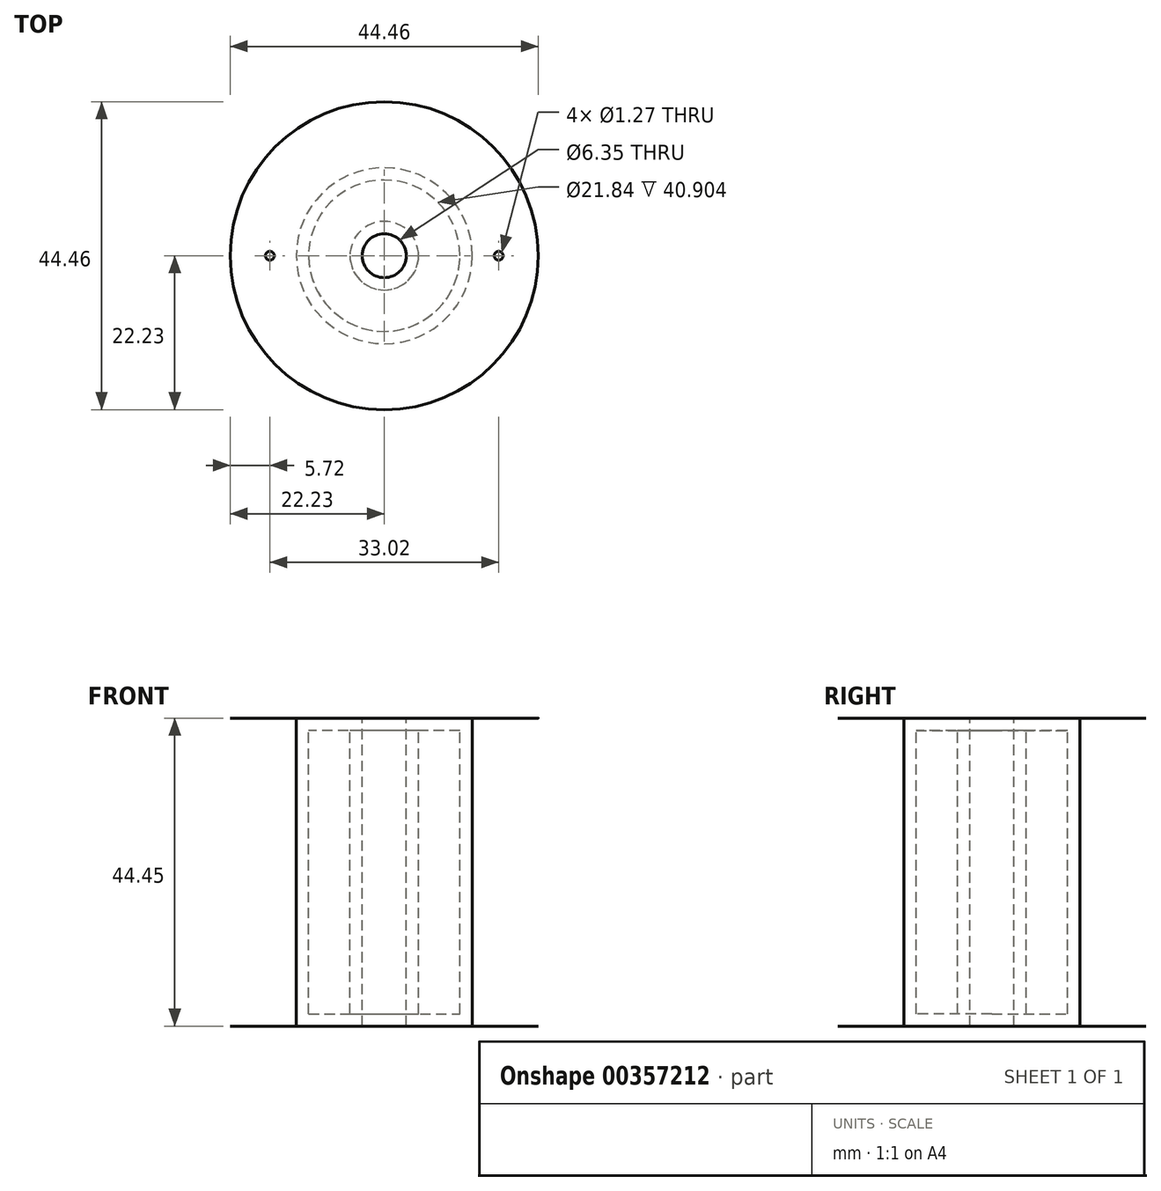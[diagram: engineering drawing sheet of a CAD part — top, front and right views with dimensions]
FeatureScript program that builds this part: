
annotation { "Feature Type Name" : "Feature", "Feature Type Description" : "" }
export const myFeature = defineFeature(function(context is Context, id is Id, definition is map)
    precondition{}
    {
        {
            var Q0;
            Q0=qCreatedBy(makeId("Top.planeOp"),FACE);
            var sketch = newSketch(context, id + "F0", { "sketchPlane" : qUnion([Q0])});
            skCircle(sketch, "E0", {"center": v(0, 0) * mm, "radius": 22.23 * mm});
            skSolve(sketch);
        }
        {
            var Q0;
            Q0=makeQuery(id+"F0.imprint","IMPRINT",FACE,{"disambiguationData":[TD([[makeQuery(id+"F0.imprint","IMPRINT",EDGE,{"derivedFrom":sQuery(id+"F0.wireOp",EDGE,"E0")}),1.0]])]});
            extrude(context, id + "F1", {"entities" : qUnion([Q0]), "depth" : 1 / 203.2 * mm});
        }
        {
            var Q0;
            Q0=makeQuery(id+"F1.opExtrude","CAP_FACE",FACE,{"disambiguationData":[OSD([sQuery(id+"F0.wireOp",EDGE,"E0")])],"isStart":true});
            var sketch = newSketch(context, id + "F2", { "sketchPlane" : qUnion([Q0])});
            skCircle(sketch, "E1", {"center": v(0, 0) * mm, "radius": 12.7 * mm});
            skSolve(sketch);
        }
        {
            var Q0;
            Q0 = qSketchRegion(id + "F2", true);
            extrude(context, id + "F3", {"entities" : qUnion([Q0]), "operationType" : NewBodyOperationType.ADD, "depth" : 44.45 * mm});
        }
        {
            var Q0;
            Q0=makeQuery(id+"F3.opExtrude","CAP_FACE",FACE,{"disambiguationData":[OSD([sQuery(id+"F2.wireOp",EDGE,"E1")])],"isStart":false});
            var sketch = newSketch(context, id + "F4", { "sketchPlane" : qUnion([Q0])});
            skCircle(sketch, "E2", {"center": v(0, 0) * mm, "radius": 22.23 * mm});
            skSolve(sketch);
        }
        {
            var Q0;
            Q0 = qSketchRegion(id + "F4", true);
            extrude(context, id + "F5", {"entities" : qUnion([Q0]), "operationType" : NewBodyOperationType.ADD, "depth" : 1 / 203.2 * mm});
        }
        {
            var Q0;
            Q0=makeQuery(id+"F1.opExtrude","CAP_FACE",FACE,{"disambiguationData":[OSD([sQuery(id+"F0.wireOp",EDGE,"E0")])],"isStart":false});
            var sketch = newSketch(context, id + "F6", { "sketchPlane" : qUnion([Q0])});
            skCircle(sketch, "E3", {"center": v(0, 0) * mm, "radius": 3.18 * mm});
            skLineSegment(sketch, "E4", {"start": v(0, 0) * mm, "end": v(22.23, 0) * mm, "construction": true});
            skCircle(sketch, "E5", {"center": v(16.51, 0) * mm, "radius": 0.64 * mm});
            skLineSegment(sketch, "E6", {"start": v(0, 0) * mm, "end": v(-22.23, 0) * mm});
            skCircle(sketch, "E7", {"center": v(-16.51, 0) * mm, "radius": 0.64 * mm});
            skSolve(sketch);
        }
        {
            var Q0;
            Q0 = qSketchRegion(id + "F6", true);
            var Q1;
            Q1=makeQuery(id+"F5.opExtrude","CAP_FACE",FACE,{"disambiguationData":[OSD([sQuery(id+"F4.wireOp",EDGE,"E2")])],"isStart":false});
            extrude(context, id + "F7", {"entities" : qUnion([Q0]), "operationType" : NewBodyOperationType.REMOVE, "endBound" : BoundingType.UP_TO_SURFACE, "oppositeDirection" : true, "endBoundEntityFace" : qUnion([Q1]), "depth" : 25.4 * mm});
        }
        {
            var Q0;
            Q0=makeQuery(id+"F3.opExtrude","SWEPT_FACE",FACE,{"disambiguationData":[OSD([sQuery(id+"F2.wireOp",EDGE,"E1")])]});
            var Q1;
            Q1=makeQuery(id+"F1.opExtrude","SWEPT_BODY",BODY,{"disambiguationData":[OSD([sQuery(id+"F0.wireOp",EDGE,"E0")])]});
            shell(context, id + "F8", {"isHollow" : true, "entities" : qUnion([Q0]), "parts" : qUnion([Q1]), "thickness" : 1.78 * mm});
        }
    });
